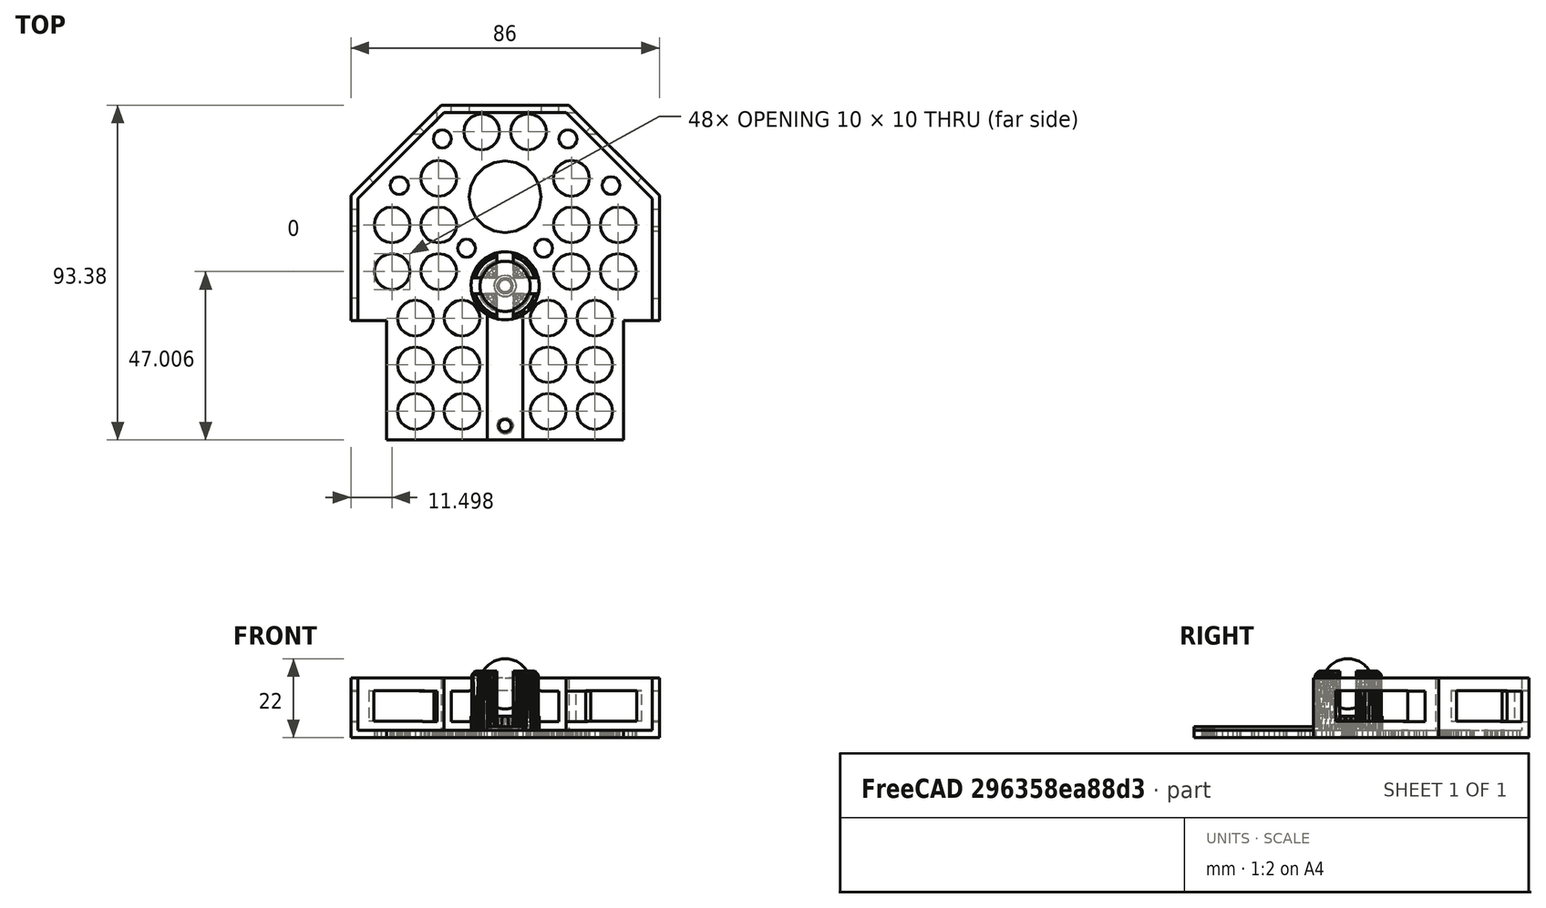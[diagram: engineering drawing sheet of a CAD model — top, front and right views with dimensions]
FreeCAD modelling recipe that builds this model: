
FCSTD DOCUMENT  (FreeCAD 0.16R6712 (Git))
Label: Soporte Sensores proximidad
License: All rights reserved
LicenseURL: http://en.wikipedia.org/wiki/All_rights_reserved
objects: Part::Box×5, Part::Cut×5, Part::Feature×2, Part::Sphere×1
note: 13 computed .brp shape members not serialized (recipe doc carries the construction recipe); baked Part::Feature solids carry a one-line shape summary decoded from their .brp

FEATURE [Part::Box] Box  label="Cubo"
  Height = 8.5
  Length = 10
  Placement = pos=(-76,45,4.5) rot=(0,0,1;0rad)
  Width = 6
FEATURE [Part::Box] Box001  label="Cubo001"
  Height = 8.5
  Length = 10
  Placement = pos=(-142,72,4.5) rot=(0,0,1;0rad)
  Width = 6
FEATURE [Part::Box] Box002  label="Cubo002"
  Height = 8.5
  Length = 30
  Placement = pos=(-128,75,4.5) rot=(0,0,1;0rad)
  Width = 7
FEATURE [Part::Feature] Addon_BallCasterWithMazeSensors001001001_solid  label="Addon_BallCasterWithMazeSensors003 (Solid)"
  shape: bbox 86 x 93.38 x 18.5 mm, 1409 faces (baked)
FEATURE [Part::Cut] Cut
  Base = -> Addon_BallCasterWithMazeSensors001001001_solid
  Tool = -> Box002
FEATURE [Part::Cut] Cut001
  Base = -> Cut
  Tool = -> Box001
FEATURE [Part::Cut] Cut002
  Base = -> Cut001
  Tool = -> Box
FEATURE [Part::Feature] Cut002001  label="Soporte escornabot sensores de proximidad"
  shape: bbox 86 x 93.38 x 18.5 mm, 1421 faces (baked)
FEATURE [Part::Sphere] Sphere  label="Bola Escornabot"
  Angle1 = -90
  Angle2 = 90
  Angle3 = 360
  Placement = pos=(-113,29.5,15) rot=(0,0,1;0rad)
  Radius = 7
FEATURE [Part::Box] Box003  label="Cubo003"
  Height = 8.5
  Length = 10
  Placement = pos=(-76,45,4.5) rot=(0,0,1;0rad)
  Width = 6
FEATURE [Part::Cut] Cut002002
  Base = -> Cut002001
  Tool = -> Box003
FEATURE [Part::Box] Box004  label="Cubo004"
  Height = 8.5
  Length = 10
  Placement = pos=(-161,45,4.5) rot=(0,0,1;0rad)
  Width = 6
FEATURE [Part::Cut] Cut002003  label="Soporte escornabot sensores de proximidad v.02"
  Base = -> Cut002002
  Tool = -> Box004
